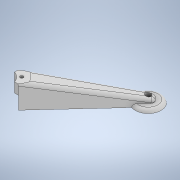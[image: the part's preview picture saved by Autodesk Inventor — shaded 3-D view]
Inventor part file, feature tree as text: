
AUTODESK INVENTOR PART (.ipt)
format: ipt  version: 2020 (Build 240168000, 168)  size: 237,568 bytes
history: native  units: mm
features: sketch x7, extrude x6, fillet x4, hole x1
ambient origin geometry x8: Origin, YZ Plane, XZ Plane, XY Plane, X Axis, Y Axis, Z Axis, Center Point
bodies: Solid1 (feature_tree)
feature tree (18):
  extrude  "Extrusion1"  Depth=10.0mm TaperAngle=0.0deg
  extrude  "Extrusion4"  Depth=10.0mm
  fillet  "Fillet2"  Radius=13.516mm
  extrude  "Extrusion5"  TaperAngle=90.0deg  [1 undecoded]
  hole  "Hole1"  [1 undecoded]
  fillet  "Fillet3"  Radius=5.0mm
  fillet  "Fillet4"  Radius=40.0mm
  extrude  "Extrusion6"  Depth=5.0mm
  fillet  "Fillet5"  Radius=8.5mm
  extrude  "Extrusion7"  TaperAngle=0.0deg  [1 undecoded]
  extrude  "Extrusion8"  Depth=5.0mm
  sketch  "Sketch1"  dims[d0=10.0mm d1=25.0mm d8=35.0mm d9=0.0mm]
  sketch  "Sketch3"  dims[d16=20.0mm d17=0.0mm d18=10.0mm d22=13.516mm]
  sketch  "Sketch6"  dims[d23=10.0mm d24=90.0deg]
  sketch  "Sketch7"  dims[d25=68.083mm d26=0.0mm]
  sketch  "Sketch8"  dims[d27=200.0mm d28=100.0mm d29=7.0mm d30=7.0mm d31=7.0mm d32=7.0mm]
  sketch  "Sketch9"  dims[d33=5.0mm d34=6.0mm d35=4.0mm d36=2.0mm d37=90.0deg d38=8.0mm d39=20.594885mm d40=5.0mm d41=5.0mm d42=40.0mm]
  sketch  "Sketch10"  dims[d43=5.0mm d44=0.0mm d45=5.0mm d46=8.5mm d47=0.0mm d48=0.0mm d49=5.0mm d50=5.0mm d51=0.0mm]
note: 3 required parameter values undecoded (feature->parameter linkage not recoverable at this tier; creation-order binding heuristic only, values carry confidence <= 0.55)
